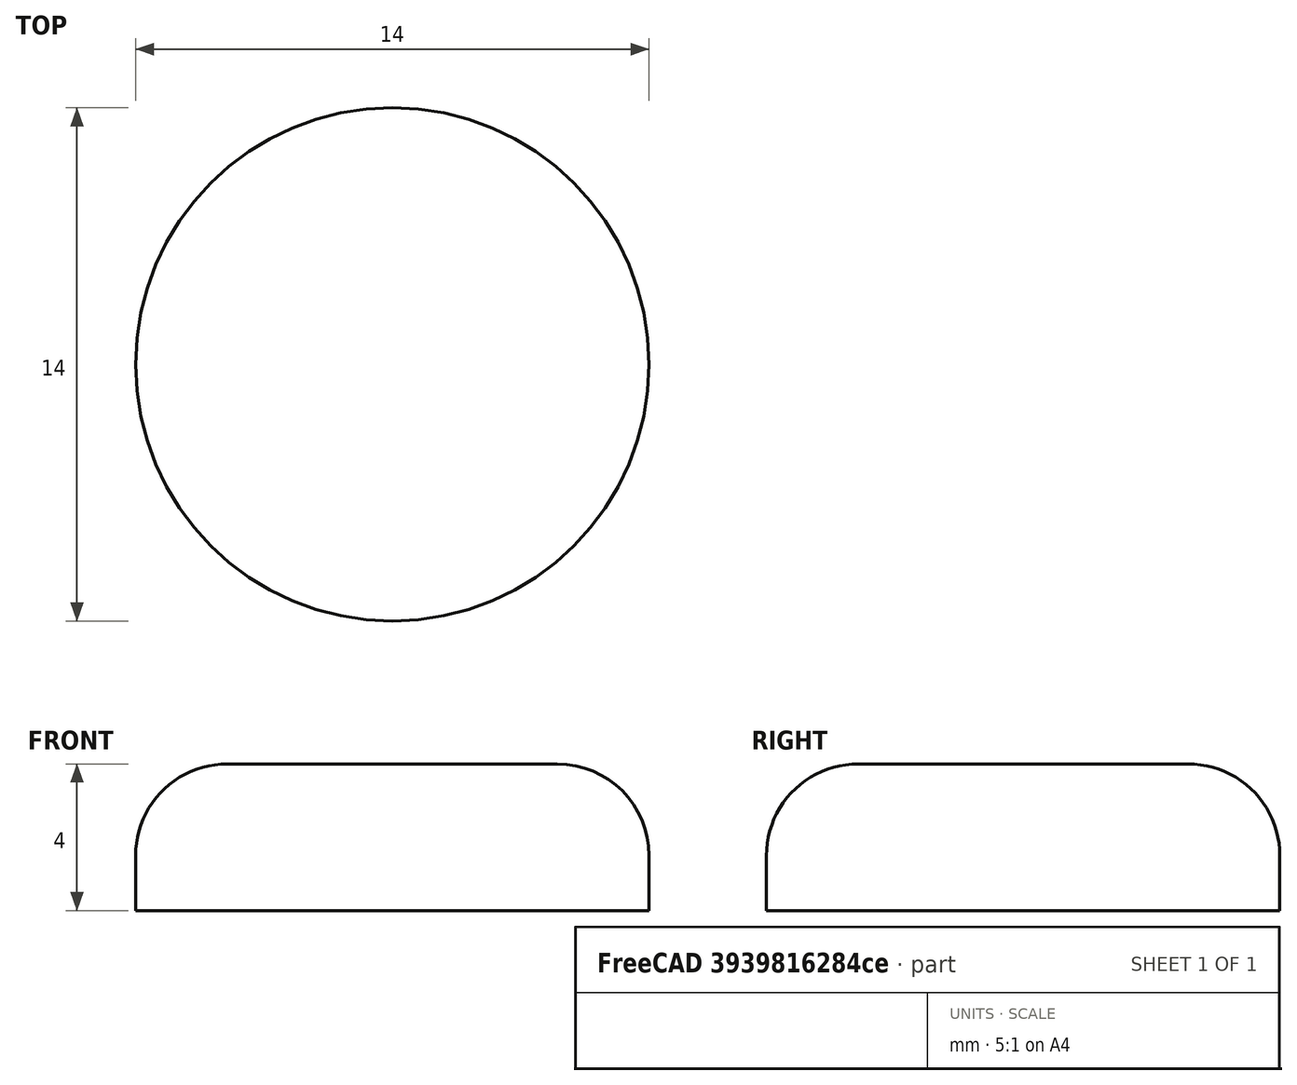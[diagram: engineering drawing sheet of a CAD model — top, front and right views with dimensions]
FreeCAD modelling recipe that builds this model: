
FCSTD DOCUMENT  (FreeCAD 1.0R39319 (Git))
Label: Button-RED-16mm
License: All rights reserved
LicenseURL: https://en.wikipedia.org/wiki/All_rights_reserved
objects: Sketcher::SketchObject×1, PartDesign::Pad×1, PartDesign::Fillet×1, PartDesign::Body×1
note: 9 computed .brp shape members not serialized (recipe doc carries the construction recipe); baked Part::Feature solids carry a one-line shape summary decoded from their .brp

FEATURE [Sketcher::SketchObject] Sketch
  ArcFitTolerance = 1e-06
  AttachmentSupport = -> [XY_Plane]
  FullyConstrained = true
  MakeInternals = false
  MapMode = 5
  sketch-geometry (1):
    g0: Circle CenterX=0 CenterY=0 CenterZ=0 NormalX=0 NormalY=0 NormalZ=1 AngleXU=0 Radius=7
  constraints (2):
    c: Diameter(g0) = 14
    c: Coincident(g0,g-1)
FEATURE [PartDesign::Pad] Pad
  Direction = (0,0,1)
  Length = 4
  Length2 = 10
  Profile = -> Sketch
  ReferenceAxis = -> Sketch [N_Axis]
  Refine = true
  Suppressed = false
  Type = 0
FEATURE [PartDesign::Fillet] Fillet
  Base = -> Pad [Edge3]
  BaseFeature = -> Pad
  Radius = 2.5
  Refine = true
  SupportTransform = false
  Suppressed = false
  UseAllEdges = false
FEATURE [PartDesign::Body] Body
  AllowCompound = false
  Group = -> [Sketch,Pad,Fillet]
  Origin = -> Origin
  Tip = -> Fillet
